FCSTD DOCUMENT  (FreeCAD 0.20R29177 +426 (Git))
Label: 097play
License: All rights reserved
LicenseURL: http://en.wikipedia.org/wiki/All_rights_reserved
objects: Sketcher::SketchObject×1, PartDesign::Body×1
note: 2 computed .brp shape members not serialized (recipe doc carries the construction recipe); baked Part::Feature solids carry a one-line shape summary decoded from their .brp

FEATURE [Sketcher::SketchObject] Sketch
  FullyConstrained = false
  MapMode = 5
  Support = -> [XY_Plane]
  sketch-geometry (4):
    g0: LineSegment StartX=-83.5995 StartY=-14.1369 StartZ=0 EndX=-33.5995 EndY=-14.7306 EndZ=0
    g1: LineSegment StartX=-33.5995 StartY=-14.7306 StartZ=0 EndX=-58.0854 EndY=28.8675 EndZ=0
    g2: LineSegment StartX=-58.0854 StartY=28.8675 StartZ=0 EndX=-83.5995 EndY=-14.1369 EndZ=0
    g3: Circle CenterX=-58.4281 CenterY=0 CenterZ=0 NormalX=0 NormalY=0 NormalZ=1 AngleXU=0 Radius=10
  constraints (7):
    c: Coincident(g0,g1)
    c: Coincident(g1,g2)
    c: Coincident(g2,g0)
    c: Equal(g0,g1)
    c: Equal(g0,g2)
    c: DistanceX(g0,g0) = 50
    c: Radius(g3) = 10
FEATURE [PartDesign::Body] Body
  Group = -> [Sketch]
  Origin = -> Origin
